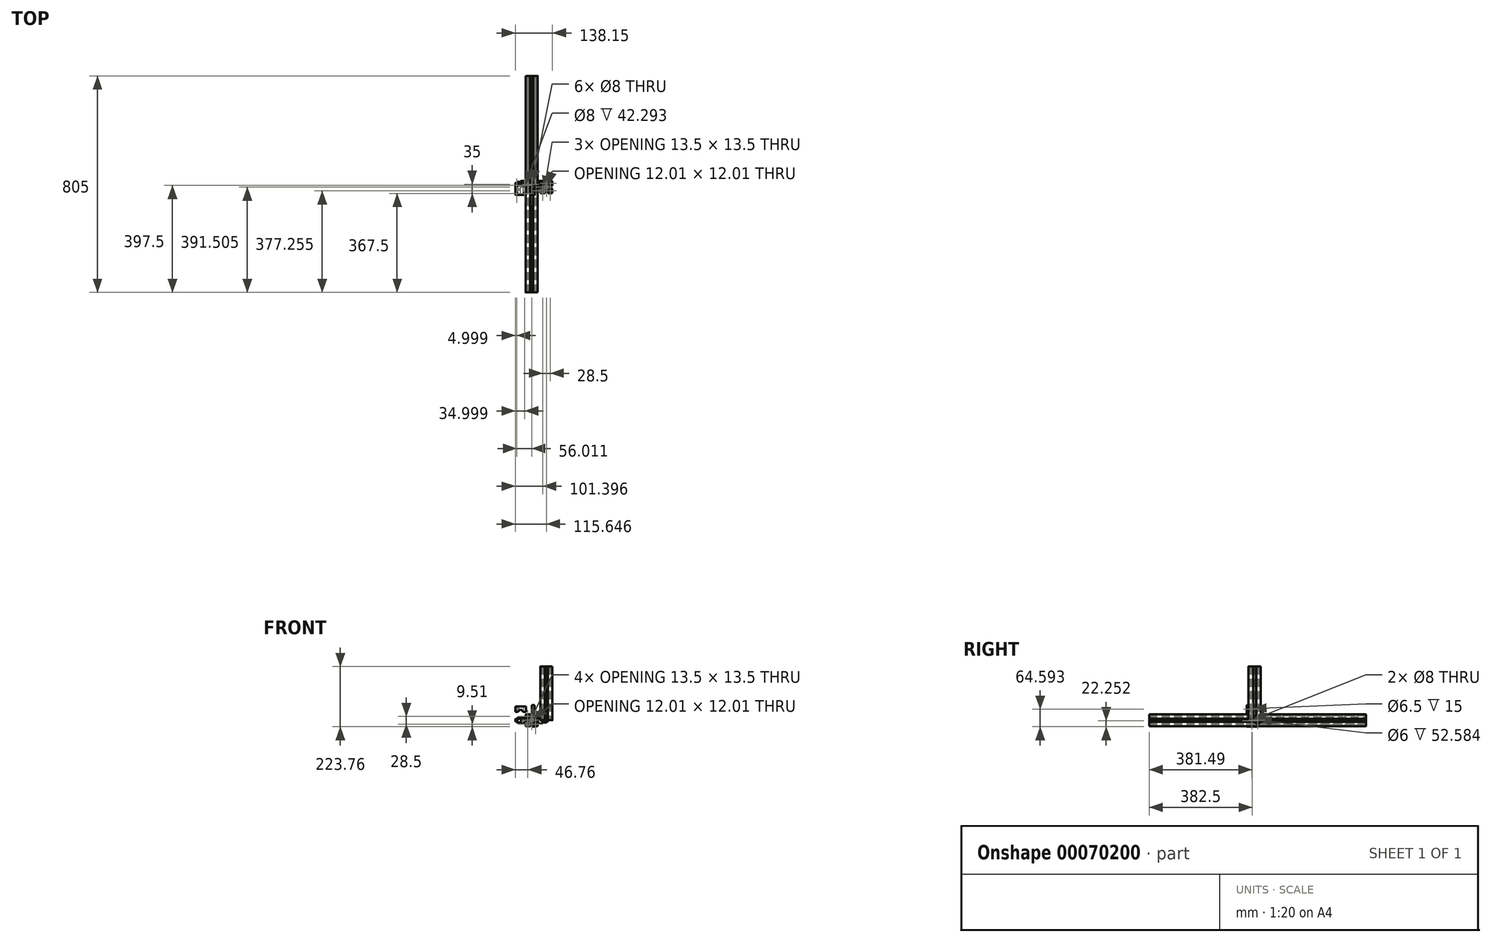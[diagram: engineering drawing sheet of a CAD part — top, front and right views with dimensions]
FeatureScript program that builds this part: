
annotation { "Feature Type Name" : "Feature", "Feature Type Description" : "" }
export const myFeature = defineFeature(function(context is Context, id is Id, definition is map)
    precondition{}
    {
        {
            var Q0;
            Q0=qCreatedBy(makeId("Front.planeOp"),FACE);
            var sketch = newSketch(context, id + "F0", { "sketchPlane" : qUnion([Q0])});
            skLineSegment(sketch, "E0", {"start": v(22.5, 19.5) * mm, "end": v(22.5, 5.8) * mm});
            skArc(sketch, "E1", {"start": v(-19.5, 22.5) * mm, "mid": v(-21.62, 21.62) * mm, "end": v(-22.5, 19.5) * mm});
            skArc(sketch, "E2", {"start": v(22.5, 19.5) * mm, "mid": v(21.62, 21.62) * mm, "end": v(19.5, 22.5) * mm});
            skLineSegment(sketch, "E3", {"start": v(-10.05, 16.5) * mm, "end": v(-5, 16.5) * mm});
            skLineSegment(sketch, "E4", {"start": v(-22.5, 5.8) * mm, "end": v(-22.5, 19.5) * mm});
            skLineSegment(sketch, "E5", {"start": v(-22.5, 5.8) * mm, "end": v(-21, 5.8) * mm});
            skLineSegment(sketch, "E6", {"start": v(-21, 5.8) * mm, "end": v(-21, 5) * mm});
            skLineSegment(sketch, "E7", {"start": v(-21, 5) * mm, "end": v(-16.5, 5) * mm});
            skLineSegment(sketch, "E8", {"start": v(-16.5, 5) * mm, "end": v(-16.5, 10.05) * mm});
            skLineSegment(sketch, "E9", {"start": v(-16.5, 10.05) * mm, "end": v(-11.68, 10.05) * mm});
            skLineSegment(sketch, "E10", {"start": v(-11.68, 10.05) * mm, "end": v(-6.41, 4.78) * mm});
            skArc(sketch, "E11", {"start": v(-6.41, 4.78) * mm, "mid": v(-8, 0) * mm, "end": v(-6.41, -4.78) * mm});
            skLineSegment(sketch, "E12", {"start": v(-6.41, -4.78) * mm, "end": v(-11.68, -10.05) * mm});
            skLineSegment(sketch, "E13", {"start": v(-11.68, -10.05) * mm, "end": v(-16.5, -10.05) * mm});
            skLineSegment(sketch, "E14", {"start": v(-16.5, -10.05) * mm, "end": v(-16.5, -5) * mm});
            skLineSegment(sketch, "E15", {"start": v(-16.5, -5) * mm, "end": v(-21, -5) * mm});
            skLineSegment(sketch, "E16", {"start": v(-21, -5) * mm, "end": v(-21, -5.8) * mm});
            skLineSegment(sketch, "E17", {"start": v(-21, -5.8) * mm, "end": v(-22.5, -5.8) * mm});
            skLineSegment(sketch, "E18", {"start": v(-22.5, -19.5) * mm, "end": v(-22.5, -5.8) * mm});
            skArc(sketch, "E19", {"start": v(-22.5, -19.5) * mm, "mid": v(-21.62, -21.62) * mm, "end": v(-19.5, -22.5) * mm});
            skLineSegment(sketch, "E20", {"start": v(-5.8, -22.5) * mm, "end": v(-19.5, -22.5) * mm});
            skLineSegment(sketch, "E21", {"start": v(-5.8, -22.5) * mm, "end": v(-5.8, -21) * mm});
            skLineSegment(sketch, "E22", {"start": v(-5.8, -21) * mm, "end": v(-5, -21) * mm});
            skLineSegment(sketch, "E23", {"start": v(-5, -21) * mm, "end": v(-5, -16.5) * mm});
            skLineSegment(sketch, "E24", {"start": v(-5, -16.5) * mm, "end": v(-10.05, -16.5) * mm});
            skLineSegment(sketch, "E25", {"start": v(-10.05, -16.5) * mm, "end": v(-10.05, -11.68) * mm});
            skLineSegment(sketch, "E26", {"start": v(-10.05, -11.68) * mm, "end": v(-4.78, -6.41) * mm});
            skArc(sketch, "E27", {"start": v(-4.78, -6.41) * mm, "mid": v(0, -8) * mm, "end": v(4.78, -6.41) * mm});
            skLineSegment(sketch, "E28", {"start": v(4.78, -6.41) * mm, "end": v(10.05, -11.68) * mm});
            skLineSegment(sketch, "E29", {"start": v(10.05, -11.68) * mm, "end": v(10.05, -16.5) * mm});
            skLineSegment(sketch, "E30", {"start": v(10.05, -16.5) * mm, "end": v(5, -16.5) * mm});
            skLineSegment(sketch, "E31", {"start": v(5, -16.5) * mm, "end": v(5, -21) * mm});
            skLineSegment(sketch, "E32", {"start": v(5, -21) * mm, "end": v(5.8, -21) * mm});
            skLineSegment(sketch, "E33", {"start": v(5.8, -21) * mm, "end": v(5.8, -22.5) * mm});
            skLineSegment(sketch, "E34", {"start": v(19.5, -22.5) * mm, "end": v(5.8, -22.5) * mm});
            skArc(sketch, "E35", {"start": v(19.5, -22.5) * mm, "mid": v(21.62, -21.62) * mm, "end": v(22.5, -19.5) * mm});
            skLineSegment(sketch, "E36", {"start": v(22.5, -5.8) * mm, "end": v(22.5, -19.5) * mm});
            skLineSegment(sketch, "E37", {"start": v(22.5, -5.8) * mm, "end": v(21, -5.8) * mm});
            skLineSegment(sketch, "E38", {"start": v(21, -5.8) * mm, "end": v(21, -5) * mm});
            skLineSegment(sketch, "E39", {"start": v(21, -5) * mm, "end": v(16.5, -5) * mm});
            skLineSegment(sketch, "E40", {"start": v(16.5, -5) * mm, "end": v(16.5, -10.05) * mm});
            skLineSegment(sketch, "E41", {"start": v(16.5, -10.05) * mm, "end": v(11.68, -10.05) * mm});
            skLineSegment(sketch, "E42", {"start": v(11.68, -10.05) * mm, "end": v(6.41, -4.78) * mm});
            skArc(sketch, "E43", {"start": v(6.41, -4.78) * mm, "mid": v(8, 0) * mm, "end": v(6.41, 4.78) * mm});
            skLineSegment(sketch, "E44", {"start": v(6.41, 4.78) * mm, "end": v(11.68, 10.05) * mm});
            skLineSegment(sketch, "E45", {"start": v(11.68, 10.05) * mm, "end": v(16.5, 10.05) * mm});
            skLineSegment(sketch, "E46", {"start": v(16.5, 10.05) * mm, "end": v(16.5, 5) * mm});
            skLineSegment(sketch, "E47", {"start": v(16.5, 5) * mm, "end": v(21, 5) * mm});
            skLineSegment(sketch, "E48", {"start": v(21, 5) * mm, "end": v(21, 5.8) * mm});
            skLineSegment(sketch, "E49", {"start": v(21, 5.8) * mm, "end": v(22.5, 5.8) * mm});
            skLineSegment(sketch, "E50", {"start": v(5, 16.5) * mm, "end": v(10.05, 16.5) * mm});
            skLineSegment(sketch, "E51", {"start": v(10.05, 16.5) * mm, "end": v(10.05, 11.68) * mm});
            skLineSegment(sketch, "E52", {"start": v(10.05, 11.68) * mm, "end": v(4.78, 6.41) * mm});
            skArc(sketch, "E53", {"start": v(4.78, 6.41) * mm, "mid": v(0, 8) * mm, "end": v(-4.78, 6.41) * mm});
            skLineSegment(sketch, "E54", {"start": v(-4.78, 6.41) * mm, "end": v(-10.05, 11.68) * mm});
            skLineSegment(sketch, "E55", {"start": v(-10.05, 11.68) * mm, "end": v(-10.05, 16.5) * mm});
            skLineSegment(sketch, "E56", {"start": v(21, 7.5) * mm, "end": v(18, 7.5) * mm});
            skLineSegment(sketch, "E57", {"start": v(18, 7.5) * mm, "end": v(18, 11.55) * mm});
            skLineSegment(sketch, "E58", {"start": v(18, 11.55) * mm, "end": v(11.55, 11.55) * mm});
            skLineSegment(sketch, "E59", {"start": v(11.55, 11.55) * mm, "end": v(11.55, 18) * mm});
            skLineSegment(sketch, "E60", {"start": v(11.55, 18) * mm, "end": v(7.5, 18) * mm});
            skLineSegment(sketch, "E61", {"start": v(7.5, 18) * mm, "end": v(7.5, 21) * mm});
            skLineSegment(sketch, "E62", {"start": v(7.5, 21) * mm, "end": v(18.5, 21) * mm});
            skArc(sketch, "E63", {"start": v(21, 18.5) * mm, "mid": v(20.27, 20.27) * mm, "end": v(18.5, 21) * mm});
            skLineSegment(sketch, "E64", {"start": v(21, 18.5) * mm, "end": v(21, 7.5) * mm});
            skLineSegment(sketch, "E65", {"start": v(7.5, -21) * mm, "end": v(7.5, -18) * mm});
            skLineSegment(sketch, "E66", {"start": v(7.5, -18) * mm, "end": v(11.55, -18) * mm});
            skLineSegment(sketch, "E67", {"start": v(11.55, -18) * mm, "end": v(11.55, -11.55) * mm});
            skLineSegment(sketch, "E68", {"start": v(11.55, -11.55) * mm, "end": v(18, -11.55) * mm});
            skLineSegment(sketch, "E69", {"start": v(18, -11.55) * mm, "end": v(18, -7.5) * mm});
            skLineSegment(sketch, "E70", {"start": v(18, -7.5) * mm, "end": v(21, -7.5) * mm});
            skLineSegment(sketch, "E71", {"start": v(21, -7.5) * mm, "end": v(21, -18.5) * mm});
            skArc(sketch, "E72", {"start": v(18.5, -21) * mm, "mid": v(20.27, -20.27) * mm, "end": v(21, -18.5) * mm});
            skLineSegment(sketch, "E73", {"start": v(18.5, -21) * mm, "end": v(7.5, -21) * mm});
            skLineSegment(sketch, "E74", {"start": v(-21, -7.5) * mm, "end": v(-18, -7.5) * mm});
            skLineSegment(sketch, "E75", {"start": v(-18, -7.5) * mm, "end": v(-18, -11.55) * mm});
            skLineSegment(sketch, "E76", {"start": v(-18, -11.55) * mm, "end": v(-11.55, -11.55) * mm});
            skLineSegment(sketch, "E77", {"start": v(-11.55, -11.55) * mm, "end": v(-11.55, -18) * mm});
            skLineSegment(sketch, "E78", {"start": v(-11.55, -18) * mm, "end": v(-7.5, -18) * mm});
            skLineSegment(sketch, "E79", {"start": v(-7.5, -18) * mm, "end": v(-7.5, -21) * mm});
            skLineSegment(sketch, "E80", {"start": v(-7.5, -21) * mm, "end": v(-18.5, -21) * mm});
            skArc(sketch, "E81", {"start": v(-21, -18.5) * mm, "mid": v(-20.27, -20.27) * mm, "end": v(-18.5, -21) * mm});
            skLineSegment(sketch, "E82", {"start": v(-21, -18.5) * mm, "end": v(-21, -7.5) * mm});
            skLineSegment(sketch, "E83", {"start": v(-7.5, 21) * mm, "end": v(-7.5, 18) * mm});
            skLineSegment(sketch, "E84", {"start": v(-7.5, 18) * mm, "end": v(-11.55, 18) * mm});
            skLineSegment(sketch, "E85", {"start": v(-11.55, 18) * mm, "end": v(-11.55, 11.55) * mm});
            skLineSegment(sketch, "E86", {"start": v(-11.55, 11.55) * mm, "end": v(-18, 11.55) * mm});
            skLineSegment(sketch, "E87", {"start": v(-18, 11.55) * mm, "end": v(-18, 7.5) * mm});
            skLineSegment(sketch, "E88", {"start": v(-18, 7.5) * mm, "end": v(-21, 7.5) * mm});
            skLineSegment(sketch, "E89", {"start": v(-21, 7.5) * mm, "end": v(-21, 18.5) * mm});
            skArc(sketch, "E90", {"start": v(-18.5, 21) * mm, "mid": v(-20.27, 20.27) * mm, "end": v(-21, 18.5) * mm});
            skLineSegment(sketch, "E91", {"start": v(-18.5, 21) * mm, "end": v(-7.5, 21) * mm});
            skArc(sketch, "E92", {"start": v(-5, 3.5) * mm, "mid": v(-5.64, 2.33) * mm, "end": v(-6, 1.06) * mm});
            skLineSegment(sketch, "E93", {"start": v(-5, 3.5) * mm, "end": v(-4.1, 2.87) * mm});
            skArc(sketch, "E94", {"start": v(-2.87, 4.1) * mm, "mid": v(-3.54, 3.54) * mm, "end": v(-4.1, 2.87) * mm});
            skLineSegment(sketch, "E95", {"start": v(-2.87, 4.1) * mm, "end": v(-3.5, 5) * mm});
            skArc(sketch, "E96", {"start": v(-1.06, 6) * mm, "mid": v(-2.33, 5.64) * mm, "end": v(-3.5, 5) * mm});
            skLineSegment(sketch, "E97", {"start": v(-1.06, 6) * mm, "end": v(-0.87, 4.92) * mm});
            skArc(sketch, "E98", {"start": v(0.87, 4.92) * mm, "mid": v(0, 5) * mm, "end": v(-0.87, 4.92) * mm});
            skLineSegment(sketch, "E99", {"start": v(0.87, 4.92) * mm, "end": v(1.06, 6) * mm});
            skArc(sketch, "E100", {"start": v(3.5, 5) * mm, "mid": v(2.33, 5.64) * mm, "end": v(1.06, 6) * mm});
            skLineSegment(sketch, "E101", {"start": v(3.5, 5) * mm, "end": v(2.87, 4.1) * mm});
            skArc(sketch, "E102", {"start": v(4.1, 2.87) * mm, "mid": v(3.54, 3.54) * mm, "end": v(2.87, 4.1) * mm});
            skLineSegment(sketch, "E103", {"start": v(4.1, 2.87) * mm, "end": v(5, 3.5) * mm});
            skArc(sketch, "E104", {"start": v(6, 1.06) * mm, "mid": v(5.64, 2.33) * mm, "end": v(5, 3.5) * mm});
            skLineSegment(sketch, "E105", {"start": v(6, 1.06) * mm, "end": v(4.92, 0.87) * mm});
            skArc(sketch, "E106", {"start": v(4.92, -0.87) * mm, "mid": v(5, 0) * mm, "end": v(4.92, 0.87) * mm});
            skLineSegment(sketch, "E107", {"start": v(4.92, -0.87) * mm, "end": v(6, -1.06) * mm});
            skArc(sketch, "E108", {"start": v(5, -3.5) * mm, "mid": v(5.64, -2.33) * mm, "end": v(6, -1.06) * mm});
            skLineSegment(sketch, "E109", {"start": v(5, -3.5) * mm, "end": v(4.1, -2.87) * mm});
            skArc(sketch, "E110", {"start": v(2.87, -4.1) * mm, "mid": v(3.54, -3.54) * mm, "end": v(4.1, -2.87) * mm});
            skLineSegment(sketch, "E111", {"start": v(2.87, -4.1) * mm, "end": v(3.5, -5) * mm});
            skArc(sketch, "E112", {"start": v(1.06, -6) * mm, "mid": v(2.33, -5.64) * mm, "end": v(3.5, -5) * mm});
            skLineSegment(sketch, "E113", {"start": v(1.06, -6) * mm, "end": v(0.87, -4.92) * mm});
            skArc(sketch, "E114", {"start": v(-0.87, -4.92) * mm, "mid": v(0, -5) * mm, "end": v(0.87, -4.92) * mm});
            skLineSegment(sketch, "E115", {"start": v(-0.87, -4.92) * mm, "end": v(-1.06, -6) * mm});
            skArc(sketch, "E116", {"start": v(-3.5, -5) * mm, "mid": v(-2.33, -5.64) * mm, "end": v(-1.06, -6) * mm});
            skLineSegment(sketch, "E117", {"start": v(-3.5, -5) * mm, "end": v(-2.87, -4.1) * mm});
            skArc(sketch, "E118", {"start": v(-4.1, -2.87) * mm, "mid": v(-3.54, -3.54) * mm, "end": v(-2.87, -4.1) * mm});
            skLineSegment(sketch, "E119", {"start": v(-4.1, -2.87) * mm, "end": v(-5, -3.5) * mm});
            skArc(sketch, "E120", {"start": v(-6, -1.06) * mm, "mid": v(-5.64, -2.33) * mm, "end": v(-5, -3.5) * mm});
            skLineSegment(sketch, "E121", {"start": v(-6, -1.06) * mm, "end": v(-4.92, -0.87) * mm});
            skArc(sketch, "E122", {"start": v(-4.92, 0.87) * mm, "mid": v(-5, 0) * mm, "end": v(-4.92, -0.87) * mm});
            skLineSegment(sketch, "E123", {"start": v(-4.92, 0.87) * mm, "end": v(-6, 1.06) * mm});
            skLineSegment(sketch, "E124.top", {"start": v(-5, 20.85) * mm, "end": v(-6, 20.85) * mm});
            skLineSegment(sketch, "E124.right", {"start": v(-6, 22.5) * mm, "end": v(-6, 20.85) * mm});
            skLineSegment(sketch, "E125.top", {"start": v(5, 20.85) * mm, "end": v(6, 20.85) * mm});
            skLineSegment(sketch, "E125.right", {"start": v(6, 22.5) * mm, "end": v(6, 20.85) * mm});
            skLineSegment(sketch, "E126", {"start": v(-19.5, 22.5) * mm, "end": v(-6, 22.5) * mm});
            skLineSegment(sketch, "E127", {"start": v(-5, 20.85) * mm, "end": v(-5, 16.5) * mm});
            skLineSegment(sketch, "E128", {"start": v(5, 20.85) * mm, "end": v(5, 16.5) * mm});
            skLineSegment(sketch, "E129", {"start": v(6, 22.5) * mm, "end": v(19.5, 22.5) * mm});
            skCircle(sketch, "E130", {"center": v(0, 0) * mm, "radius": 4 * mm});
            skSolve(sketch);
        }
        {
            var Q0;
            Q0=makeQuery(id+"F0.imprint","IMPRINT",FACE,{"disambiguationData":[TD([[makeQuery(id+"F0.imprint","IMPRINT",EDGE,{"derivedFrom":sQuery(id+"F0.wireOp",EDGE,"E0")}),-1.0]])]});
            extrude(context, id + "F1", {"entities" : qUnion([Q0]), "endBound" : BoundingType.SYMMETRIC, "depth" : 805 * mm});
        }
        {
            var Q0;
            Q0=qCreatedBy(makeId("Right.planeOp"),FACE);
            var sketch = newSketch(context, id + "F2", { "sketchPlane" : qUnion([Q0])});
            skLineSegment(sketch, "E131.bottom", {"start": v(-40.87, 56.24) * mm, "end": v(-0.87, 56.24) * mm});
            skLineSegment(sketch, "E131.top", {"start": v(-40.87, -23.76) * mm, "end": v(-0.87, -23.76) * mm});
            skLineSegment(sketch, "E131.left", {"start": v(-40.87, 56.24) * mm, "end": v(-40.87, -23.76) * mm});
            skLineSegment(sketch, "E131.right", {"start": v(-0.87, 56.24) * mm, "end": v(-0.87, -23.76) * mm});
            skLineSegment(sketch, "E132", {"start": v(-40.87, 3) * mm, "end": v(0, 3) * mm});
            skLineSegment(sketch, "E133", {"start": v(-40.87, -6.5) * mm, "end": v(-0.87, -6.5) * mm});
            skLineSegment(sketch, "E134.bottom", {"start": v(-25.77, 56.24) * mm, "end": v(-15.97, 56.24) * mm});
            skLineSegment(sketch, "E134.top", {"start": v(-25.77, 26.24) * mm, "end": v(-15.97, 26.24) * mm});
            skLineSegment(sketch, "E134.left", {"start": v(-25.77, 56.24) * mm, "end": v(-25.77, 26.24) * mm});
            skLineSegment(sketch, "E134.right", {"start": v(-15.97, 56.24) * mm, "end": v(-15.97, 26.24) * mm});
            skCircle(sketch, "E135", {"center": v(-20.87, 41.24) * mm, "radius": 4 * mm});
            skPoint(sketch, "E135.centerSnap0", {"position": v(-25.77, 41.24) * mm});
            skLineSegment(sketch, "E136", {"start": v(-20.87, 56.24) * mm, "end": v(-20.87, -7.98) * mm, "construction": true});
            skPoint(sketch, "E136.endSnap0", {"position": v(-20.87, 26.24) * mm});
            skCircle(sketch, "E137", {"center": v(-21, -1.5) * mm, "radius": 4 * mm});
            skLineSegment(sketch, "E138", {"start": v(-0.87, 33.08) * mm, "end": v(-15.97, 33.08) * mm, "construction": true});
            skLineSegment(sketch, "E139", {"start": v(-25.77, 32.73) * mm, "end": v(-40.87, 32.73) * mm, "construction": true});
            skSolve(sketch);
        }
        {
            var Q0;
            Q0=makeQuery(id+"F2.imprint","IMPRINT",FACE,{"disambiguationData":[TD([[makeQuery(id+"F2.imprint","IMPRINT",EDGE,{"derivedFrom":sQuery(id+"F2.wireOp",EDGE,"E134.bottom")}),-1.0]])]});
            var Q1;
            {var subQ0=sQuery(id+"F2.wireOp",EDGE,"E133");Q1=makeQuery(id+"F2.imprint","IMPRINT",FACE,{"disambiguationData":[TD([[makeQuery(id+"F2.imprint","IMPRINT",EDGE,{"derivedFrom":subQ0}),1.0]])]});}
            extrude(context, id + "F3", {"entities" : qUnion([Q0, Q1]), "depth" : 14 * mm});
        }
        {
            var Q0;
            {var subQ0=sQuery(id+"F2.wireOp",EDGE,"E131.top");Q0=makeQuery(id+"F2.imprint","IMPRINT",FACE,{"disambiguationData":[TD([[makeQuery(id+"F2.imprint","IMPRINT",EDGE,{"derivedFrom":subQ0}),1.0]])]});}
            var Q1;
            Q1=makeQuery(id+"F2.imprint","IMPRINT",FACE,{"disambiguationData":[TD([[makeQuery(id+"F2.imprint","IMPRINT",EDGE,{"derivedFrom":sQuery(id+"F2.wireOp",EDGE,"E134.top")}),-1.0]])]});
            extrude(context, id + "F4", {"entities" : qUnion([Q0, Q1]), "operationType" : NewBodyOperationType.ADD, "depth" : 10 * mm});
        }
        {
            var Q0;
            Q0=qCreatedBy(makeId("Top.planeOp"),FACE);
            var sketch = newSketch(context, id + "F5", { "sketchPlane" : qUnion([Q0])});
            skLineSegment(sketch, "E140", {"start": v(77.14, 8.5) * mm, "end": v(77.14, -5.2) * mm});
            skArc(sketch, "E141", {"start": v(35.14, 11.5) * mm, "mid": v(33.01, 10.63) * mm, "end": v(32.14, 8.5) * mm});
            skArc(sketch, "E142", {"start": v(77.14, 8.5) * mm, "mid": v(76.26, 10.63) * mm, "end": v(74.14, 11.5) * mm});
            skLineSegment(sketch, "E143", {"start": v(44.59, 5.5) * mm, "end": v(49.64, 5.5) * mm});
            skLineSegment(sketch, "E144", {"start": v(32.14, -5.2) * mm, "end": v(32.14, 8.5) * mm});
            skLineSegment(sketch, "E145", {"start": v(32.14, -5.2) * mm, "end": v(33.64, -5.2) * mm});
            skLineSegment(sketch, "E146", {"start": v(33.64, -5.2) * mm, "end": v(33.64, -6) * mm});
            skLineSegment(sketch, "E147", {"start": v(33.64, -6) * mm, "end": v(38.14, -6) * mm});
            skLineSegment(sketch, "E148", {"start": v(38.14, -6) * mm, "end": v(38.14, -0.95) * mm});
            skLineSegment(sketch, "E149", {"start": v(38.14, -0.95) * mm, "end": v(42.96, -0.95) * mm});
            skLineSegment(sketch, "E150", {"start": v(42.96, -0.95) * mm, "end": v(48.22, -6.21) * mm});
            skArc(sketch, "E151", {"start": v(48.22, -6.21) * mm, "mid": v(46.64, -11) * mm, "end": v(48.22, -15.78) * mm});
            skLineSegment(sketch, "E152", {"start": v(48.22, -15.78) * mm, "end": v(42.96, -21.05) * mm});
            skLineSegment(sketch, "E153", {"start": v(42.96, -21.05) * mm, "end": v(38.14, -21.05) * mm});
            skLineSegment(sketch, "E154", {"start": v(38.14, -21.05) * mm, "end": v(38.14, -16) * mm});
            skLineSegment(sketch, "E155", {"start": v(38.14, -16) * mm, "end": v(33.64, -16) * mm});
            skLineSegment(sketch, "E156", {"start": v(33.64, -16) * mm, "end": v(33.64, -16.8) * mm});
            skLineSegment(sketch, "E157", {"start": v(33.64, -16.8) * mm, "end": v(32.14, -16.8) * mm});
            skLineSegment(sketch, "E158", {"start": v(32.14, -30.5) * mm, "end": v(32.14, -16.8) * mm});
            skArc(sketch, "E159", {"start": v(32.14, -30.5) * mm, "mid": v(33.01, -32.62) * mm, "end": v(35.14, -33.5) * mm});
            skLineSegment(sketch, "E160", {"start": v(48.84, -33.5) * mm, "end": v(35.14, -33.5) * mm});
            skLineSegment(sketch, "E161", {"start": v(48.84, -33.5) * mm, "end": v(48.84, -32) * mm});
            skLineSegment(sketch, "E162", {"start": v(48.84, -32) * mm, "end": v(49.64, -32) * mm});
            skLineSegment(sketch, "E163", {"start": v(49.64, -32) * mm, "end": v(49.64, -27.5) * mm});
            skLineSegment(sketch, "E164", {"start": v(49.64, -27.5) * mm, "end": v(44.59, -27.5) * mm});
            skLineSegment(sketch, "E165", {"start": v(44.59, -27.5) * mm, "end": v(44.59, -22.67) * mm});
            skLineSegment(sketch, "E166", {"start": v(44.59, -22.67) * mm, "end": v(49.85, -17.4) * mm});
            skArc(sketch, "E167", {"start": v(49.85, -17.4) * mm, "mid": v(54.64, -19) * mm, "end": v(59.42, -17.4) * mm});
            skLineSegment(sketch, "E168", {"start": v(59.42, -17.4) * mm, "end": v(64.69, -22.67) * mm});
            skLineSegment(sketch, "E169", {"start": v(64.69, -22.67) * mm, "end": v(64.69, -27.5) * mm});
            skLineSegment(sketch, "E170", {"start": v(64.69, -27.5) * mm, "end": v(59.64, -27.5) * mm});
            skLineSegment(sketch, "E171", {"start": v(59.64, -27.5) * mm, "end": v(59.64, -32) * mm});
            skLineSegment(sketch, "E172", {"start": v(59.64, -32) * mm, "end": v(60.44, -32) * mm});
            skLineSegment(sketch, "E173", {"start": v(60.44, -32) * mm, "end": v(60.44, -33.5) * mm});
            skLineSegment(sketch, "E174", {"start": v(74.14, -33.5) * mm, "end": v(60.44, -33.5) * mm});
            skArc(sketch, "E175", {"start": v(74.14, -33.5) * mm, "mid": v(76.26, -32.62) * mm, "end": v(77.14, -30.5) * mm});
            skLineSegment(sketch, "E176", {"start": v(77.14, -16.8) * mm, "end": v(77.14, -30.5) * mm});
            skLineSegment(sketch, "E177", {"start": v(77.14, -16.8) * mm, "end": v(75.64, -16.8) * mm});
            skLineSegment(sketch, "E178", {"start": v(75.64, -16.8) * mm, "end": v(75.64, -16) * mm});
            skLineSegment(sketch, "E179", {"start": v(75.64, -16) * mm, "end": v(71.14, -16) * mm});
            skLineSegment(sketch, "E180", {"start": v(71.14, -16) * mm, "end": v(71.14, -21.05) * mm});
            skLineSegment(sketch, "E181", {"start": v(71.14, -21.05) * mm, "end": v(66.31, -21.05) * mm});
            skLineSegment(sketch, "E182", {"start": v(66.31, -21.05) * mm, "end": v(61.05, -15.78) * mm});
            skArc(sketch, "E183", {"start": v(61.05, -15.78) * mm, "mid": v(62.64, -11) * mm, "end": v(61.05, -6.21) * mm});
            skLineSegment(sketch, "E184", {"start": v(61.05, -6.21) * mm, "end": v(66.31, -0.95) * mm});
            skLineSegment(sketch, "E185", {"start": v(66.31, -0.95) * mm, "end": v(71.14, -0.95) * mm});
            skLineSegment(sketch, "E186", {"start": v(71.14, -0.95) * mm, "end": v(71.14, -6) * mm});
            skLineSegment(sketch, "E187", {"start": v(71.14, -6) * mm, "end": v(75.64, -6) * mm});
            skLineSegment(sketch, "E188", {"start": v(75.64, -6) * mm, "end": v(75.64, -5.2) * mm});
            skLineSegment(sketch, "E189", {"start": v(75.64, -5.2) * mm, "end": v(77.14, -5.2) * mm});
            skLineSegment(sketch, "E190", {"start": v(59.64, 5.5) * mm, "end": v(64.69, 5.5) * mm});
            skLineSegment(sketch, "E191", {"start": v(64.69, 5.5) * mm, "end": v(64.69, 0.68) * mm});
            skLineSegment(sketch, "E192", {"start": v(64.69, 0.68) * mm, "end": v(59.42, -4.58) * mm});
            skArc(sketch, "E193", {"start": v(59.42, -4.58) * mm, "mid": v(54.64, -3) * mm, "end": v(49.85, -4.58) * mm});
            skLineSegment(sketch, "E194", {"start": v(49.85, -4.58) * mm, "end": v(44.59, 0.68) * mm});
            skLineSegment(sketch, "E195", {"start": v(44.59, 0.68) * mm, "end": v(44.59, 5.5) * mm});
            skLineSegment(sketch, "E196", {"start": v(75.64, -3.5) * mm, "end": v(72.64, -3.5) * mm});
            skLineSegment(sketch, "E197", {"start": v(72.64, -3.5) * mm, "end": v(72.64, 0.55) * mm});
            skLineSegment(sketch, "E198", {"start": v(72.64, 0.55) * mm, "end": v(66.19, 0.55) * mm});
            skLineSegment(sketch, "E199", {"start": v(66.19, 0.55) * mm, "end": v(66.19, 7) * mm});
            skLineSegment(sketch, "E200", {"start": v(66.19, 7) * mm, "end": v(62.14, 7) * mm});
            skLineSegment(sketch, "E201", {"start": v(62.14, 7) * mm, "end": v(62.14, 10) * mm});
            skLineSegment(sketch, "E202", {"start": v(62.14, 10) * mm, "end": v(73.14, 10) * mm});
            skArc(sketch, "E203", {"start": v(75.64, 7.5) * mm, "mid": v(74.9, 9.27) * mm, "end": v(73.14, 10) * mm});
            skLineSegment(sketch, "E204", {"start": v(75.64, 7.5) * mm, "end": v(75.64, -3.5) * mm});
            skLineSegment(sketch, "E205", {"start": v(62.14, -32) * mm, "end": v(62.14, -29) * mm});
            skLineSegment(sketch, "E206", {"start": v(62.14, -29) * mm, "end": v(66.19, -29) * mm});
            skLineSegment(sketch, "E207", {"start": v(66.19, -29) * mm, "end": v(66.19, -22.55) * mm});
            skLineSegment(sketch, "E208", {"start": v(66.19, -22.55) * mm, "end": v(72.64, -22.55) * mm});
            skLineSegment(sketch, "E209", {"start": v(72.64, -22.55) * mm, "end": v(72.64, -18.5) * mm});
            skLineSegment(sketch, "E210", {"start": v(72.64, -18.5) * mm, "end": v(75.64, -18.5) * mm});
            skLineSegment(sketch, "E211", {"start": v(75.64, -18.5) * mm, "end": v(75.64, -29.5) * mm});
            skArc(sketch, "E212", {"start": v(73.14, -32) * mm, "mid": v(74.9, -31.26) * mm, "end": v(75.64, -29.5) * mm});
            skLineSegment(sketch, "E213", {"start": v(73.14, -32) * mm, "end": v(62.14, -32) * mm});
            skLineSegment(sketch, "E214", {"start": v(33.64, -18.5) * mm, "end": v(36.64, -18.5) * mm});
            skLineSegment(sketch, "E215", {"start": v(36.64, -18.5) * mm, "end": v(36.64, -22.55) * mm});
            skLineSegment(sketch, "E216", {"start": v(36.64, -22.55) * mm, "end": v(43.09, -22.55) * mm});
            skLineSegment(sketch, "E217", {"start": v(43.09, -22.55) * mm, "end": v(43.09, -29) * mm});
            skLineSegment(sketch, "E218", {"start": v(43.09, -29) * mm, "end": v(47.14, -29) * mm});
            skLineSegment(sketch, "E219", {"start": v(47.14, -29) * mm, "end": v(47.14, -32) * mm});
            skLineSegment(sketch, "E220", {"start": v(47.14, -32) * mm, "end": v(36.14, -32) * mm});
            skArc(sketch, "E221", {"start": v(33.64, -29.5) * mm, "mid": v(34.37, -31.26) * mm, "end": v(36.14, -32) * mm});
            skLineSegment(sketch, "E222", {"start": v(33.64, -29.5) * mm, "end": v(33.64, -18.5) * mm});
            skLineSegment(sketch, "E223", {"start": v(47.14, 10) * mm, "end": v(47.14, 7) * mm});
            skLineSegment(sketch, "E224", {"start": v(47.14, 7) * mm, "end": v(43.09, 7) * mm});
            skLineSegment(sketch, "E225", {"start": v(43.09, 7) * mm, "end": v(43.09, 0.55) * mm});
            skLineSegment(sketch, "E226", {"start": v(43.09, 0.55) * mm, "end": v(36.64, 0.55) * mm});
            skLineSegment(sketch, "E227", {"start": v(36.64, 0.55) * mm, "end": v(36.64, -3.5) * mm});
            skLineSegment(sketch, "E228", {"start": v(36.64, -3.5) * mm, "end": v(33.64, -3.5) * mm});
            skLineSegment(sketch, "E229", {"start": v(33.64, -3.5) * mm, "end": v(33.64, 7.5) * mm});
            skArc(sketch, "E230", {"start": v(36.14, 10) * mm, "mid": v(34.37, 9.27) * mm, "end": v(33.64, 7.5) * mm});
            skLineSegment(sketch, "E231", {"start": v(36.14, 10) * mm, "end": v(47.14, 10) * mm});
            skArc(sketch, "E232", {"start": v(49.64, -7.5) * mm, "mid": v(49, -8.66) * mm, "end": v(48.63, -9.94) * mm});
            skLineSegment(sketch, "E233", {"start": v(49.64, -7.5) * mm, "end": v(50.54, -8.13) * mm});
            skArc(sketch, "E234", {"start": v(51.77, -6.9) * mm, "mid": v(51.1, -7.46) * mm, "end": v(50.54, -8.13) * mm});
            skLineSegment(sketch, "E235", {"start": v(51.77, -6.9) * mm, "end": v(51.14, -6) * mm});
            skArc(sketch, "E236", {"start": v(53.58, -4.99) * mm, "mid": v(52.3, -5.36) * mm, "end": v(51.14, -6) * mm});
            skLineSegment(sketch, "E237", {"start": v(53.58, -4.99) * mm, "end": v(53.77, -6.07) * mm});
            skArc(sketch, "E238", {"start": v(55.5, -6.07) * mm, "mid": v(54.64, -6) * mm, "end": v(53.77, -6.07) * mm});
            skLineSegment(sketch, "E239", {"start": v(55.5, -6.07) * mm, "end": v(55.7, -4.99) * mm});
            skArc(sketch, "E240", {"start": v(58.13, -6) * mm, "mid": v(56.97, -5.36) * mm, "end": v(55.7, -4.99) * mm});
            skLineSegment(sketch, "E241", {"start": v(58.13, -6) * mm, "end": v(57.5, -6.9) * mm});
            skArc(sketch, "E242", {"start": v(58.73, -8.13) * mm, "mid": v(58.17, -7.46) * mm, "end": v(57.5, -6.9) * mm});
            skLineSegment(sketch, "E243", {"start": v(58.73, -8.13) * mm, "end": v(59.63, -7.5) * mm});
            skArc(sketch, "E244", {"start": v(60.64, -9.94) * mm, "mid": v(60.27, -8.66) * mm, "end": v(59.63, -7.5) * mm});
            skLineSegment(sketch, "E245", {"start": v(60.64, -9.94) * mm, "end": v(59.56, -10.13) * mm});
            skArc(sketch, "E246", {"start": v(59.56, -11.86) * mm, "mid": v(59.64, -11) * mm, "end": v(59.56, -10.13) * mm});
            skLineSegment(sketch, "E247", {"start": v(59.56, -11.86) * mm, "end": v(60.64, -12.05) * mm});
            skArc(sketch, "E248", {"start": v(59.63, -14.5) * mm, "mid": v(60.27, -13.33) * mm, "end": v(60.64, -12.05) * mm});
            skLineSegment(sketch, "E249", {"start": v(59.63, -14.5) * mm, "end": v(58.73, -13.86) * mm});
            skArc(sketch, "E250", {"start": v(57.5, -15.1) * mm, "mid": v(58.17, -14.53) * mm, "end": v(58.73, -13.86) * mm});
            skLineSegment(sketch, "E251", {"start": v(57.5, -15.1) * mm, "end": v(58.13, -16) * mm});
            skArc(sketch, "E252", {"start": v(55.7, -17) * mm, "mid": v(56.97, -16.63) * mm, "end": v(58.13, -16) * mm});
            skLineSegment(sketch, "E253", {"start": v(55.7, -17) * mm, "end": v(55.5, -15.92) * mm});
            skArc(sketch, "E254", {"start": v(53.77, -15.92) * mm, "mid": v(54.64, -16) * mm, "end": v(55.5, -15.92) * mm});
            skLineSegment(sketch, "E255", {"start": v(53.77, -15.92) * mm, "end": v(53.58, -17) * mm});
            skArc(sketch, "E256", {"start": v(51.14, -16) * mm, "mid": v(52.3, -16.63) * mm, "end": v(53.58, -17) * mm});
            skLineSegment(sketch, "E257", {"start": v(51.14, -16) * mm, "end": v(51.77, -15.1) * mm});
            skArc(sketch, "E258", {"start": v(50.54, -13.86) * mm, "mid": v(51.1, -14.53) * mm, "end": v(51.77, -15.1) * mm});
            skLineSegment(sketch, "E259", {"start": v(50.54, -13.86) * mm, "end": v(49.64, -14.5) * mm});
            skArc(sketch, "E260", {"start": v(48.63, -12.05) * mm, "mid": v(49, -13.33) * mm, "end": v(49.64, -14.5) * mm});
            skLineSegment(sketch, "E261", {"start": v(48.63, -12.05) * mm, "end": v(49.71, -11.86) * mm});
            skArc(sketch, "E262", {"start": v(49.71, -10.13) * mm, "mid": v(49.64, -11) * mm, "end": v(49.71, -11.86) * mm});
            skLineSegment(sketch, "E263", {"start": v(49.71, -10.13) * mm, "end": v(48.63, -9.94) * mm});
            skLineSegment(sketch, "E264.top", {"start": v(49.64, 9.86) * mm, "end": v(48.63, 9.86) * mm});
            skLineSegment(sketch, "E264.right", {"start": v(48.63, 11.5) * mm, "end": v(48.63, 9.86) * mm});
            skLineSegment(sketch, "E265.top", {"start": v(59.64, 9.86) * mm, "end": v(60.65, 9.86) * mm});
            skLineSegment(sketch, "E265.right", {"start": v(60.65, 11.5) * mm, "end": v(60.65, 9.86) * mm});
            skLineSegment(sketch, "E266", {"start": v(35.14, 11.5) * mm, "end": v(48.63, 11.5) * mm});
            skLineSegment(sketch, "E267", {"start": v(49.64, 9.86) * mm, "end": v(49.64, 5.5) * mm});
            skLineSegment(sketch, "E268", {"start": v(59.64, 9.86) * mm, "end": v(59.64, 5.5) * mm});
            skLineSegment(sketch, "E269", {"start": v(60.65, 11.5) * mm, "end": v(74.14, 11.5) * mm});
            skCircle(sketch, "E270", {"center": v(54.64, -11) * mm, "radius": 4 * mm});
            skSolve(sketch);
        }
        {
            var Q0;
            Q0=makeQuery(id+"F5.imprint","IMPRINT",FACE,{"disambiguationData":[TD([[makeQuery(id+"F5.imprint","IMPRINT",EDGE,{"derivedFrom":sQuery(id+"F5.wireOp",EDGE,"E140")}),-1.0]])]});
            extrude(context, id + "F6", {"entities" : qUnion([Q0]), "depth" : 200 * mm});
        }
        {
            var Q0;
            Q0=qCreatedBy(makeId("Right.planeOp"),FACE);
            var sketch = newSketch(context, id + "F7", { "sketchPlane" : qUnion([Q0])});
            skCircle(sketch, "E271", {"center": v(0, 0) * mm, "radius": 5 * mm});
            skCircle(sketch, "E272", {"center": v(0, 0) * mm, "radius": 8 * mm});
            skCircle(sketch, "E273", {"center": v(0, 0) * mm, "radius": 12.5 * mm});
            skCircle(sketch, "E274", {"center": v(0, 0) * mm, "radius": 3 * mm});
            skSolve(sketch);
        }
        {
            var Q0;
            Q0=makeQuery(id+"F7.imprint","IMPRINT",FACE,{"disambiguationData":[TD([[makeQuery(id+"F7.imprint","IMPRINT",EDGE,{"derivedFrom":sQuery(id+"F7.wireOp",EDGE,"E271")}),1.0]])]});
            extrude(context, id + "F8", {"entities" : qUnion([Q0]), "endBound" : BoundingType.SYMMETRIC, "depth" : 120 * mm});
        }
        {
            var Q0;
            Q0=makeQuery(id+"F7.imprint","IMPRINT",FACE,{"disambiguationData":[TD([[makeQuery(id+"F7.imprint","IMPRINT",EDGE,{"derivedFrom":sQuery(id+"F7.wireOp",EDGE,"E271")}),-1.0]])]});
            extrude(context, id + "F9", {"entities" : qUnion([Q0]), "operationType" : NewBodyOperationType.ADD, "endBound" : BoundingType.SYMMETRIC, "depth" : 110 * mm});
        }
        {
            var Q0;
            Q0=qCreatedBy(makeId("Front.planeOp"),FACE);
            var sketch = newSketch(context, id + "F10", { "sketchPlane" : qUnion([Q0])});
            skCircle(sketch, "E275", {"center": v(0, 0) * mm, "radius": 4 * mm});
            skLineSegment(sketch, "E276", {"start": v(-5, 0) * mm, "end": v(-4, 0) * mm, "construction": true});
            skSolve(sketch);
        }
        {
            var Q0;
            Q0=qCreatedBy(makeId("Top.planeOp"),FACE);
            var sketch = newSketch(context, id + "F11", { "sketchPlane" : qUnion([Q0])});
            skLineSegment(sketch, "E277", {"start": v(-21.8, -6) * mm, "end": v(23.24, -6) * mm});
            skLineSegment(sketch, "E278", {"start": v(23.24, -6) * mm, "end": v(23.24, -13) * mm});
            skLineSegment(sketch, "E279", {"start": v(23.24, -13) * mm, "end": v(-21.8, -13) * mm});
            skLineSegment(sketch, "E280", {"start": v(-21.8, -13) * mm, "end": v(-21.8, -6) * mm});
            skLineSegment(sketch, "E281", {"start": v(-4.98, -13) * mm, "end": v(-4.98, -6) * mm});
            skLineSegment(sketch, "E282", {"start": v(5.02, -6) * mm, "end": v(5.02, -13) * mm});
            skSolve(sketch);
        }
        {
            var Q0;
            Q0=makeQuery(id+"F7.imprint","IMPRINT",FACE,{"disambiguationData":[TD([[makeQuery(id+"F7.imprint","IMPRINT",EDGE,{"derivedFrom":sQuery(id+"F7.wireOp",EDGE,"E272")}),-1.0]])]});
            extrude(context, id + "F12", {"entities" : qUnion([Q0]), "operationType" : NewBodyOperationType.ADD, "endBound" : BoundingType.SYMMETRIC, "depth" : 80 * mm});
        }
        {
            var Q0;
            {var subQ0=sQuery(id+"F11.wireOp",EDGE,"E280");Q0=makeQuery(id+"F11.imprint","IMPRINT",FACE,{"disambiguationData":[TD([[makeQuery(id+"F11.imprint","IMPRINT",EDGE,{"derivedFrom":subQ0}),-1.0]])]});}
            var Q1;
            {var subQ0=sQuery(id+"F11.wireOp",EDGE,"E278");Q1=makeQuery(id+"F11.imprint","IMPRINT",FACE,{"disambiguationData":[TD([[makeQuery(id+"F11.imprint","IMPRINT",EDGE,{"derivedFrom":subQ0}),-1.0]])]});}
            extrude(context, id + "F13", {"entities" : qUnion([Q0, Q1]), "operationType" : NewBodyOperationType.REMOVE, "endBound" : BoundingType.THROUGH_ALL, "depth" : 25 * mm, "hasSecondDirection" : true, "secondDirectionBound" : SecondDirectionBoundingType.THROUGH_ALL, "secondDirectionOppositeDirection" : true, "secondDirectionDepth" : 25 * mm});
        }
        {
            var Q0;
            Q0 = qSketchRegion(id + "F10", true);
            extrude(context, id + "F14", {"entities" : qUnion([Q0]), "operationType" : NewBodyOperationType.REMOVE, "endBound" : BoundingType.THROUGH_ALL, "oppositeDirection" : true, "depth" : 25 * mm, "hasSecondDirection" : true, "secondDirectionBound" : SecondDirectionBoundingType.THROUGH_ALL, "secondDirectionOppositeDirection" : false, "secondDirectionDepth" : 25 * mm});
        }
        {
            var Q0;
            Q0=makeQuery(id+"F1.opExtrude","SWEPT_BODY",BODY,{"disambiguationData":[OSD([sQuery(id+"F0.wireOp",EDGE,"E0"),sQuery(id+"F0.wireOp",EDGE,"E1"),sQuery(id+"F0.wireOp",EDGE,"E2"),sQuery(id+"F0.wireOp",EDGE,"E3"),sQuery(id+"F0.wireOp",EDGE,"E4"),sQuery(id+"F0.wireOp",EDGE,"E5"),sQuery(id+"F0.wireOp",EDGE,"E6"),sQuery(id+"F0.wireOp",EDGE,"E7"),sQuery(id+"F0.wireOp",EDGE,"E8"),sQuery(id+"F0.wireOp",EDGE,"E9"),sQuery(id+"F0.wireOp",EDGE,"E10"),sQuery(id+"F0.wireOp",EDGE,"E11"),sQuery(id+"F0.wireOp",EDGE,"E12"),sQuery(id+"F0.wireOp",EDGE,"E13"),sQuery(id+"F0.wireOp",EDGE,"E14"),sQuery(id+"F0.wireOp",EDGE,"E15"),sQuery(id+"F0.wireOp",EDGE,"E16"),sQuery(id+"F0.wireOp",EDGE,"E17"),sQuery(id+"F0.wireOp",EDGE,"E18"),sQuery(id+"F0.wireOp",EDGE,"E19"),sQuery(id+"F0.wireOp",EDGE,"E20"),sQuery(id+"F0.wireOp",EDGE,"E21"),sQuery(id+"F0.wireOp",EDGE,"E22"),sQuery(id+"F0.wireOp",EDGE,"E23"),sQuery(id+"F0.wireOp",EDGE,"E24"),sQuery(id+"F0.wireOp",EDGE,"E25"),sQuery(id+"F0.wireOp",EDGE,"E26"),sQuery(id+"F0.wireOp",EDGE,"E27"),sQuery(id+"F0.wireOp",EDGE,"E28"),sQuery(id+"F0.wireOp",EDGE,"E29"),sQuery(id+"F0.wireOp",EDGE,"E30"),sQuery(id+"F0.wireOp",EDGE,"E31"),sQuery(id+"F0.wireOp",EDGE,"E32"),sQuery(id+"F0.wireOp",EDGE,"E33"),sQuery(id+"F0.wireOp",EDGE,"E34"),sQuery(id+"F0.wireOp",EDGE,"E35"),sQuery(id+"F0.wireOp",EDGE,"E36"),sQuery(id+"F0.wireOp",EDGE,"E37"),sQuery(id+"F0.wireOp",EDGE,"E38"),sQuery(id+"F0.wireOp",EDGE,"E39"),sQuery(id+"F0.wireOp",EDGE,"E40"),sQuery(id+"F0.wireOp",EDGE,"E41"),sQuery(id+"F0.wireOp",EDGE,"E42"),sQuery(id+"F0.wireOp",EDGE,"E43"),sQuery(id+"F0.wireOp",EDGE,"E44"),sQuery(id+"F0.wireOp",EDGE,"E45"),sQuery(id+"F0.wireOp",EDGE,"E46"),sQuery(id+"F0.wireOp",EDGE,"E47"),sQuery(id+"F0.wireOp",EDGE,"E48"),sQuery(id+"F0.wireOp",EDGE,"E49"),sQuery(id+"F0.wireOp",EDGE,"E50"),sQuery(id+"F0.wireOp",EDGE,"E51"),sQuery(id+"F0.wireOp",EDGE,"E52"),sQuery(id+"F0.wireOp",EDGE,"E53"),sQuery(id+"F0.wireOp",EDGE,"E54"),sQuery(id+"F0.wireOp",EDGE,"E55"),sQuery(id+"F0.wireOp",EDGE,"E56"),sQuery(id+"F0.wireOp",EDGE,"E57"),sQuery(id+"F0.wireOp",EDGE,"E58"),sQuery(id+"F0.wireOp",EDGE,"E59"),sQuery(id+"F0.wireOp",EDGE,"E60"),sQuery(id+"F0.wireOp",EDGE,"E61"),sQuery(id+"F0.wireOp",EDGE,"E62"),sQuery(id+"F0.wireOp",EDGE,"E63"),sQuery(id+"F0.wireOp",EDGE,"E64"),sQuery(id+"F0.wireOp",EDGE,"E65"),sQuery(id+"F0.wireOp",EDGE,"E66"),sQuery(id+"F0.wireOp",EDGE,"E67"),sQuery(id+"F0.wireOp",EDGE,"E68"),sQuery(id+"F0.wireOp",EDGE,"E69"),sQuery(id+"F0.wireOp",EDGE,"E70"),sQuery(id+"F0.wireOp",EDGE,"E71"),sQuery(id+"F0.wireOp",EDGE,"E72"),sQuery(id+"F0.wireOp",EDGE,"E73"),sQuery(id+"F0.wireOp",EDGE,"E74"),sQuery(id+"F0.wireOp",EDGE,"E75"),sQuery(id+"F0.wireOp",EDGE,"E76"),sQuery(id+"F0.wireOp",EDGE,"E77"),sQuery(id+"F0.wireOp",EDGE,"E78"),sQuery(id+"F0.wireOp",EDGE,"E79"),sQuery(id+"F0.wireOp",EDGE,"E80"),sQuery(id+"F0.wireOp",EDGE,"E81"),sQuery(id+"F0.wireOp",EDGE,"E82"),sQuery(id+"F0.wireOp",EDGE,"E83"),sQuery(id+"F0.wireOp",EDGE,"E84"),sQuery(id+"F0.wireOp",EDGE,"E85"),sQuery(id+"F0.wireOp",EDGE,"E86"),sQuery(id+"F0.wireOp",EDGE,"E87"),sQuery(id+"F0.wireOp",EDGE,"E88"),sQuery(id+"F0.wireOp",EDGE,"E89"),sQuery(id+"F0.wireOp",EDGE,"E90"),sQuery(id+"F0.wireOp",EDGE,"E91"),sQuery(id+"F0.wireOp",EDGE,"E92"),sQuery(id+"F0.wireOp",EDGE,"E93"),sQuery(id+"F0.wireOp",EDGE,"E94"),sQuery(id+"F0.wireOp",EDGE,"E95"),sQuery(id+"F0.wireOp",EDGE,"E96"),sQuery(id+"F0.wireOp",EDGE,"E97"),sQuery(id+"F0.wireOp",EDGE,"E98"),sQuery(id+"F0.wireOp",EDGE,"E99"),sQuery(id+"F0.wireOp",EDGE,"E100"),sQuery(id+"F0.wireOp",EDGE,"E101"),sQuery(id+"F0.wireOp",EDGE,"E102"),sQuery(id+"F0.wireOp",EDGE,"E103"),sQuery(id+"F0.wireOp",EDGE,"E104"),sQuery(id+"F0.wireOp",EDGE,"E105"),sQuery(id+"F0.wireOp",EDGE,"E106"),sQuery(id+"F0.wireOp",EDGE,"E107"),sQuery(id+"F0.wireOp",EDGE,"E108"),sQuery(id+"F0.wireOp",EDGE,"E109"),sQuery(id+"F0.wireOp",EDGE,"E110"),sQuery(id+"F0.wireOp",EDGE,"E111"),sQuery(id+"F0.wireOp",EDGE,"E112"),sQuery(id+"F0.wireOp",EDGE,"E113"),sQuery(id+"F0.wireOp",EDGE,"E114"),sQuery(id+"F0.wireOp",EDGE,"E115"),sQuery(id+"F0.wireOp",EDGE,"E116"),sQuery(id+"F0.wireOp",EDGE,"E117"),sQuery(id+"F0.wireOp",EDGE,"E118"),sQuery(id+"F0.wireOp",EDGE,"E119"),sQuery(id+"F0.wireOp",EDGE,"E120"),sQuery(id+"F0.wireOp",EDGE,"E121"),sQuery(id+"F0.wireOp",EDGE,"E122"),sQuery(id+"F0.wireOp",EDGE,"E123"),sQuery(id+"F0.wireOp",EDGE,"E124.top"),sQuery(id+"F0.wireOp",EDGE,"E124.right"),sQuery(id+"F0.wireOp",EDGE,"E125.top"),sQuery(id+"F0.wireOp",EDGE,"E125.right"),sQuery(id+"F0.wireOp",EDGE,"E126"),sQuery(id+"F0.wireOp",EDGE,"E127"),sQuery(id+"F0.wireOp",EDGE,"E128"),sQuery(id+"F0.wireOp",EDGE,"E129")])]});
            transform(context, id + "F15", {"entities" : qUnion([Q0]), "transformType" : TransformType.TRANSLATION_3D, "dx" : 125.05 * mm, "dy" : 0 * mm, "dz" : 0 * mm, "makeCopy" : true});
        }
        {
            var Q0;
            Q0=makeQuery(id+"F15.opPattern","COPY",BODY,{"derivedFrom":makeQuery(id+"F1.opExtrude","SWEPT_BODY",BODY,{"disambiguationData":[OSD([sQuery(id+"F0.wireOp",EDGE,"E0"),sQuery(id+"F0.wireOp",EDGE,"E1"),sQuery(id+"F0.wireOp",EDGE,"E2"),sQuery(id+"F0.wireOp",EDGE,"E3"),sQuery(id+"F0.wireOp",EDGE,"E4"),sQuery(id+"F0.wireOp",EDGE,"E5"),sQuery(id+"F0.wireOp",EDGE,"E6"),sQuery(id+"F0.wireOp",EDGE,"E7"),sQuery(id+"F0.wireOp",EDGE,"E8"),sQuery(id+"F0.wireOp",EDGE,"E9"),sQuery(id+"F0.wireOp",EDGE,"E10"),sQuery(id+"F0.wireOp",EDGE,"E11"),sQuery(id+"F0.wireOp",EDGE,"E12"),sQuery(id+"F0.wireOp",EDGE,"E13"),sQuery(id+"F0.wireOp",EDGE,"E14"),sQuery(id+"F0.wireOp",EDGE,"E15"),sQuery(id+"F0.wireOp",EDGE,"E16"),sQuery(id+"F0.wireOp",EDGE,"E17"),sQuery(id+"F0.wireOp",EDGE,"E18"),sQuery(id+"F0.wireOp",EDGE,"E19"),sQuery(id+"F0.wireOp",EDGE,"E20"),sQuery(id+"F0.wireOp",EDGE,"E21"),sQuery(id+"F0.wireOp",EDGE,"E22"),sQuery(id+"F0.wireOp",EDGE,"E23"),sQuery(id+"F0.wireOp",EDGE,"E24"),sQuery(id+"F0.wireOp",EDGE,"E25"),sQuery(id+"F0.wireOp",EDGE,"E26"),sQuery(id+"F0.wireOp",EDGE,"E27"),sQuery(id+"F0.wireOp",EDGE,"E28"),sQuery(id+"F0.wireOp",EDGE,"E29"),sQuery(id+"F0.wireOp",EDGE,"E30"),sQuery(id+"F0.wireOp",EDGE,"E31"),sQuery(id+"F0.wireOp",EDGE,"E32"),sQuery(id+"F0.wireOp",EDGE,"E33"),sQuery(id+"F0.wireOp",EDGE,"E34"),sQuery(id+"F0.wireOp",EDGE,"E35"),sQuery(id+"F0.wireOp",EDGE,"E36"),sQuery(id+"F0.wireOp",EDGE,"E37"),sQuery(id+"F0.wireOp",EDGE,"E38"),sQuery(id+"F0.wireOp",EDGE,"E39"),sQuery(id+"F0.wireOp",EDGE,"E40"),sQuery(id+"F0.wireOp",EDGE,"E41"),sQuery(id+"F0.wireOp",EDGE,"E42"),sQuery(id+"F0.wireOp",EDGE,"E43"),sQuery(id+"F0.wireOp",EDGE,"E44"),sQuery(id+"F0.wireOp",EDGE,"E45"),sQuery(id+"F0.wireOp",EDGE,"E46"),sQuery(id+"F0.wireOp",EDGE,"E47"),sQuery(id+"F0.wireOp",EDGE,"E48"),sQuery(id+"F0.wireOp",EDGE,"E49"),sQuery(id+"F0.wireOp",EDGE,"E50"),sQuery(id+"F0.wireOp",EDGE,"E51"),sQuery(id+"F0.wireOp",EDGE,"E52"),sQuery(id+"F0.wireOp",EDGE,"E53"),sQuery(id+"F0.wireOp",EDGE,"E54"),sQuery(id+"F0.wireOp",EDGE,"E55"),sQuery(id+"F0.wireOp",EDGE,"E56"),sQuery(id+"F0.wireOp",EDGE,"E57"),sQuery(id+"F0.wireOp",EDGE,"E58"),sQuery(id+"F0.wireOp",EDGE,"E59"),sQuery(id+"F0.wireOp",EDGE,"E60"),sQuery(id+"F0.wireOp",EDGE,"E61"),sQuery(id+"F0.wireOp",EDGE,"E62"),sQuery(id+"F0.wireOp",EDGE,"E63"),sQuery(id+"F0.wireOp",EDGE,"E64"),sQuery(id+"F0.wireOp",EDGE,"E65"),sQuery(id+"F0.wireOp",EDGE,"E66"),sQuery(id+"F0.wireOp",EDGE,"E67"),sQuery(id+"F0.wireOp",EDGE,"E68"),sQuery(id+"F0.wireOp",EDGE,"E69"),sQuery(id+"F0.wireOp",EDGE,"E70"),sQuery(id+"F0.wireOp",EDGE,"E71"),sQuery(id+"F0.wireOp",EDGE,"E72"),sQuery(id+"F0.wireOp",EDGE,"E73"),sQuery(id+"F0.wireOp",EDGE,"E74"),sQuery(id+"F0.wireOp",EDGE,"E75"),sQuery(id+"F0.wireOp",EDGE,"E76"),sQuery(id+"F0.wireOp",EDGE,"E77"),sQuery(id+"F0.wireOp",EDGE,"E78"),sQuery(id+"F0.wireOp",EDGE,"E79"),sQuery(id+"F0.wireOp",EDGE,"E80"),sQuery(id+"F0.wireOp",EDGE,"E81"),sQuery(id+"F0.wireOp",EDGE,"E82"),sQuery(id+"F0.wireOp",EDGE,"E83"),sQuery(id+"F0.wireOp",EDGE,"E84"),sQuery(id+"F0.wireOp",EDGE,"E85"),sQuery(id+"F0.wireOp",EDGE,"E86"),sQuery(id+"F0.wireOp",EDGE,"E87"),sQuery(id+"F0.wireOp",EDGE,"E88"),sQuery(id+"F0.wireOp",EDGE,"E89"),sQuery(id+"F0.wireOp",EDGE,"E90"),sQuery(id+"F0.wireOp",EDGE,"E91"),sQuery(id+"F0.wireOp",EDGE,"E92"),sQuery(id+"F0.wireOp",EDGE,"E93"),sQuery(id+"F0.wireOp",EDGE,"E94"),sQuery(id+"F0.wireOp",EDGE,"E95"),sQuery(id+"F0.wireOp",EDGE,"E96"),sQuery(id+"F0.wireOp",EDGE,"E97"),sQuery(id+"F0.wireOp",EDGE,"E98"),sQuery(id+"F0.wireOp",EDGE,"E99"),sQuery(id+"F0.wireOp",EDGE,"E100"),sQuery(id+"F0.wireOp",EDGE,"E101"),sQuery(id+"F0.wireOp",EDGE,"E102"),sQuery(id+"F0.wireOp",EDGE,"E103"),sQuery(id+"F0.wireOp",EDGE,"E104"),sQuery(id+"F0.wireOp",EDGE,"E105"),sQuery(id+"F0.wireOp",EDGE,"E106"),sQuery(id+"F0.wireOp",EDGE,"E107"),sQuery(id+"F0.wireOp",EDGE,"E108"),sQuery(id+"F0.wireOp",EDGE,"E109"),sQuery(id+"F0.wireOp",EDGE,"E110"),sQuery(id+"F0.wireOp",EDGE,"E111"),sQuery(id+"F0.wireOp",EDGE,"E112"),sQuery(id+"F0.wireOp",EDGE,"E113"),sQuery(id+"F0.wireOp",EDGE,"E114"),sQuery(id+"F0.wireOp",EDGE,"E115"),sQuery(id+"F0.wireOp",EDGE,"E116"),sQuery(id+"F0.wireOp",EDGE,"E117"),sQuery(id+"F0.wireOp",EDGE,"E118"),sQuery(id+"F0.wireOp",EDGE,"E119"),sQuery(id+"F0.wireOp",EDGE,"E120"),sQuery(id+"F0.wireOp",EDGE,"E121"),sQuery(id+"F0.wireOp",EDGE,"E122"),sQuery(id+"F0.wireOp",EDGE,"E123"),sQuery(id+"F0.wireOp",EDGE,"E124.top"),sQuery(id+"F0.wireOp",EDGE,"E124.right"),sQuery(id+"F0.wireOp",EDGE,"E125.top"),sQuery(id+"F0.wireOp",EDGE,"E125.right"),sQuery(id+"F0.wireOp",EDGE,"E126"),sQuery(id+"F0.wireOp",EDGE,"E127"),sQuery(id+"F0.wireOp",EDGE,"E128"),sQuery(id+"F0.wireOp",EDGE,"E129")])]}),"instanceName":"1"});
            deleteBodies(context, id + "F16", {"entities" : qUnion([Q0])});
        }
        {
            var Q0;
            Q0=makeQuery(id+"F0.imprint","IMPRINT",FACE,{"disambiguationData":[TD([[makeQuery(id+"F0.imprint","IMPRINT",EDGE,{"derivedFrom":sQuery(id+"F0.wireOp",EDGE,"E0")}),-1.0]])]});
            extrude(context, id + "F17", {"entities" : qUnion([Q0]), "depth" : 100 * mm});
        }
        {
            var Q0;
            {var subQ0=sQuery(id+"F2.wireOp",EDGE,"E131.top");Q0=makeQuery(id+"F2.imprint","IMPRINT",FACE,{"disambiguationData":[TD([[makeQuery(id+"F2.imprint","IMPRINT",EDGE,{"derivedFrom":subQ0}),1.0]])]});}
            var Q1;
            Q1=makeQuery(id+"F2.imprint","IMPRINT",FACE,{"disambiguationData":[TD([[makeQuery(id+"F2.imprint","IMPRINT",EDGE,{"derivedFrom":sQuery(id+"F2.wireOp",EDGE,"E134.top")}),-1.0]])]});
            var Q2;
            Q2=makeQuery(id+"F2.imprint","IMPRINT",FACE,{"disambiguationData":[TD([[makeQuery(id+"F2.imprint","IMPRINT",EDGE,{"derivedFrom":sQuery(id+"F2.wireOp",EDGE,"E134.bottom")}),-1.0]])]});
            extrude(context, id + "F18", {"entities" : qUnion([Q0, Q1, Q2]), "depth" : 10 * mm});
        }
        {
            var Q0;
            {var subQ0=sQuery(id+"F2.wireOp",EDGE,"E133");Q0=makeQuery(id+"F2.imprint","IMPRINT",FACE,{"disambiguationData":[TD([[makeQuery(id+"F2.imprint","IMPRINT",EDGE,{"derivedFrom":subQ0}),1.0]])]});}
            extrude(context, id + "F19", {"entities" : qUnion([Q0]), "operationType" : NewBodyOperationType.ADD, "depth" : 14 * mm});
        }
        {
            var Q0;
            Q0=qCreatedBy(makeId("Front.planeOp"),FACE);
            var sketch = newSketch(context, id + "F20", { "sketchPlane" : qUnion([Q0])});
            skLineSegment(sketch, "E283.bottom", {"start": v(-61.01, 50.83) * mm, "end": v(-21.01, 50.83) * mm});
            skLineSegment(sketch, "E283.top", {"start": v(-61.01, 30.83) * mm, "end": v(-51.01, 30.83) * mm});
            skLineSegment(sketch, "E283.left", {"start": v(-61.01, 50.83) * mm, "end": v(-61.01, 30.83) * mm});
            skLineSegment(sketch, "E283.right", {"start": v(-21.01, 50.83) * mm, "end": v(-21.01, 30.83) * mm});
            skLineSegment(sketch, "E284", {"start": v(-41.01, 40.83) * mm, "end": v(-51.01, 30.83) * mm});
            skPoint(sketch, "E285.orphan", {"position": v(-41.01, 40.83) * mm});
            skLineSegment(sketch, "E286", {"start": v(-41.01, 52.38) * mm, "end": v(-41.01, 24.45) * mm, "construction": true});
            skPoint(sketch, "E286.startSnap0", {"position": v(-41.01, 50.83) * mm});
            skPoint(sketch, "E286.endSnap0", {"position": v(-41.01, 30.83) * mm});
            skLineSegment(sketch, "E287.MirrorCS", {"start": v(-41.01, 40.83) * mm, "end": v(-31.01, 30.83) * mm});
            skLineSegment(sketch, "E288.trimOffspring", {"start": v(-31.01, 30.83) * mm, "end": v(-21.01, 30.83) * mm});
            skPoint(sketch, "E289.left.end.orphan", {"position": v(-38.94, 42.9) * mm});
            skPoint(sketch, "E289.bottom.start.orphan", {"position": v(-38.94, 40.83) * mm});
            skPoint(sketch, "E290.orphan", {"position": v(-43.08, 42.9) * mm});
            skPoint(sketch, "E291.MirrorCS.start.orphan", {"position": v(-43.08, 40.83) * mm});
            skSolve(sketch);
        }
        {
            var Q0;
            Q0=makeQuery(id+"F20.imprint","IMPRINT",FACE,{"disambiguationData":[TD([[makeQuery(id+"F20.imprint","IMPRINT",EDGE,{"derivedFrom":sQuery(id+"F20.wireOp",EDGE,"E283.bottom")}),-1.0]])]});
            extrude(context, id + "F21", {"entities" : qUnion([Q0]), "depth" : 40 * mm});
        }
        {
            var Q0;
            Q0=makeQuery(id+"F21.opExtrude","SWEPT_FACE",FACE,{"disambiguationData":[OSD([sQuery(id+"F20.wireOp",EDGE,"E283.bottom")])]});
            var sketch = newSketch(context, id + "F22", { "sketchPlane" : qUnion([Q0])});
            skCircle(sketch, "E292", {"center": v(-56.01, -5) * mm, "radius": 4 * mm});
            skCircle(sketch, "E293.0.1.0", {"center": v(-56.01, -35) * mm, "radius": 4 * mm});
            skCircle(sketch, "E293.1.0.0", {"center": v(-26.01, -5) * mm, "radius": 4 * mm});
            skCircle(sketch, "E293.1.1.0", {"center": v(-26.01, -35) * mm, "radius": 4 * mm});
            skLineSegment(sketch, "E293.direction1", {"start": v(-56.01, -5) * mm, "end": v(-26.01, -5) * mm, "construction": true});
            skLineSegment(sketch, "E293.direction2", {"start": v(-56.01, -5) * mm, "end": v(-56.01, -35) * mm, "construction": true});
            skSolve(sketch);
        }
        {
            var Q0;
            Q0=makeQuery(id+"F22.imprint","IMPRINT",FACE,{"disambiguationData":[TD([[makeQuery(id+"F22.imprint","IMPRINT",EDGE,{"derivedFrom":sQuery(id+"F22.wireOp",EDGE,"E292")}),1.0]])]});
            var Q1;
            Q1=makeQuery(id+"F22.imprint","IMPRINT",FACE,{"disambiguationData":[TD([[makeQuery(id+"F22.imprint","IMPRINT",EDGE,{"derivedFrom":sQuery(id+"F22.wireOp",EDGE,"E293.1.0.0")}),1.0]])]});
            var Q2;
            Q2=makeQuery(id+"F22.imprint","IMPRINT",FACE,{"disambiguationData":[TD([[makeQuery(id+"F22.imprint","IMPRINT",EDGE,{"derivedFrom":sQuery(id+"F22.wireOp",EDGE,"E293.0.1.0")}),1.0]])]});
            var Q3;
            Q3=makeQuery(id+"F22.imprint","IMPRINT",FACE,{"disambiguationData":[TD([[makeQuery(id+"F22.imprint","IMPRINT",EDGE,{"derivedFrom":sQuery(id+"F22.wireOp",EDGE,"E293.1.1.0")}),1.0]])]});
            extrude(context, id + "F23", {"entities" : qUnion([Q0, Q1, Q2, Q3]), "operationType" : NewBodyOperationType.REMOVE, "endBound" : BoundingType.THROUGH_ALL, "oppositeDirection" : true, "depth" : 25 * mm});
        }
        {
            var Q0;
            Q0=makeQuery(id+"F21.opExtrude","SWEPT_FACE",FACE,{"disambiguationData":[OSD([sQuery(id+"F20.wireOp",EDGE,"E283.left")])]});
            var sketch = newSketch(context, id + "F24", { "sketchPlane" : qUnion([Q0])});
            skCircle(sketch, "E294", {"center": v(20, 40.83) * mm, "radius": 3.25 * mm});
            skLineSegment(sketch, "E295", {"start": v(0, 40.83) * mm, "end": v(40, 40.83) * mm, "construction": true});
            skLineSegment(sketch, "E296", {"start": v(20, 50.83) * mm, "end": v(20, 30.83) * mm});
            skSolve(sketch);
        }
        {
            var Q0;
            {var subQ0=sQuery(id+"F24.wireOp",EDGE,"E296");var subQ1=sQuery(id+"F24.wireOp",EDGE,"E294");var subQ2=makeQuery(id+"F24.imprint","INTERSECT",VERTEX,{"disambiguationData":[OD(0.0)],"derivedFrom":[subQ1,subQ0]});Q0=makeQuery(id+"F24.imprint","IMPRINT",FACE,{"disambiguationData":[TD([[makeQuery(id+"F24.imprint","IMPRINT",EDGE,{"disambiguationData":[TD([[subQ2,1.0]])],"derivedFrom":subQ1}),1.0]])]});}
            var Q1;
            {var subQ0=sQuery(id+"F24.wireOp",EDGE,"E296");var subQ1=sQuery(id+"F24.wireOp",EDGE,"E294");var subQ2=makeQuery(id+"F24.imprint","INTERSECT",VERTEX,{"disambiguationData":[OD(0.0)],"derivedFrom":[subQ1,subQ0]});Q1=makeQuery(id+"F24.imprint","IMPRINT",FACE,{"disambiguationData":[TD([[makeQuery(id+"F24.imprint","IMPRINT",EDGE,{"disambiguationData":[TD([[subQ2,-1.0]])],"derivedFrom":subQ1}),1.0]])]});}
            extrude(context, id + "F25", {"entities" : qUnion([Q0, Q1]), "operationType" : NewBodyOperationType.REMOVE, "oppositeDirection" : true, "depth" : 15 * mm});
        }
        {
            var Q0;
            Q0=qCreatedBy(makeId("Front.planeOp"),FACE);
            var sketch = newSketch(context, id + "F26", { "sketchPlane" : qUnion([Q0])});
            skCircle(sketch, "E297", {"center": v(0, 0) * mm, "radius": 12.5 * mm});
            skSolve(sketch);
        }
        {
            var Q0;
            Q0=qCreatedBy(makeId("Right.planeOp"),FACE);
            var sketch = newSketch(context, id + "F27", { "sketchPlane" : qUnion([Q0])});
            skLineSegment(sketch, "E298", {"start": v(-21.83, 14.06) * mm, "end": v(23.2, 14.06) * mm});
            skLineSegment(sketch, "E299", {"start": v(23.2, 14.06) * mm, "end": v(23.2, 5.19) * mm});
            skLineSegment(sketch, "E300", {"start": v(23.2, 5.19) * mm, "end": v(-21.83, 5.19) * mm});
            skLineSegment(sketch, "E301", {"start": v(-21.83, 5.19) * mm, "end": v(-21.83, 14.06) * mm});
            skLineSegment(sketch, "E302", {"start": v(-4.75, 5.19) * mm, "end": v(-4.75, 14.06) * mm});
            skLineSegment(sketch, "E303", {"start": v(5.25, 14.06) * mm, "end": v(5.25, 5.19) * mm});
            skLineSegment(sketch, "E304", {"start": v(0, 27.66) * mm, "end": v(0, -7.5) * mm, "construction": true});
            skSolve(sketch);
        }
        {
            var Q0;
            Q0=makeQuery(id+"F26.imprint","IMPRINT",FACE,{"disambiguationData":[TD([[makeQuery(id+"F26.imprint","IMPRINT",EDGE,{"derivedFrom":sQuery(id+"F26.wireOp",EDGE,"E297")}),1.0]])]});
            extrude(context, id + "F28", {"entities" : qUnion([Q0]), "endBound" : BoundingType.SYMMETRIC, "depth" : 160 * mm});
        }
        {
            var Q0;
            {var subQ0=sQuery(id+"F27.wireOp",EDGE,"E299");Q0=makeQuery(id+"F27.imprint","IMPRINT",FACE,{"disambiguationData":[TD([[makeQuery(id+"F27.imprint","IMPRINT",EDGE,{"derivedFrom":subQ0}),-1.0]])]});}
            var Q1;
            {var subQ0=sQuery(id+"F27.wireOp",EDGE,"E301");Q1=makeQuery(id+"F27.imprint","IMPRINT",FACE,{"disambiguationData":[TD([[makeQuery(id+"F27.imprint","IMPRINT",EDGE,{"derivedFrom":subQ0}),-1.0]])]});}
            extrude(context, id + "F29", {"entities" : qUnion([Q0, Q1]), "operationType" : NewBodyOperationType.REMOVE, "endBound" : BoundingType.THROUGH_ALL, "oppositeDirection" : true, "depth" : 25 * mm, "hasSecondDirection" : true, "secondDirectionBound" : SecondDirectionBoundingType.THROUGH_ALL, "secondDirectionOppositeDirection" : false, "secondDirectionDepth" : 25 * mm});
        }
        {
            var Q0;
            Q0=qCreatedBy(makeId("Top.planeOp"),FACE);
            var sketch = newSketch(context, id + "F30", { "sketchPlane" : qUnion([Q0])});
            skCircle(sketch, "E305", {"center": v(0, 0) * mm, "radius": 4 * mm});
            skSolve(sketch);
        }
        {
            var Q0;
            Q0=makeQuery(id+"F30.imprint","IMPRINT",FACE,{"disambiguationData":[TD([[makeQuery(id+"F30.imprint","IMPRINT",EDGE,{"derivedFrom":sQuery(id+"F30.wireOp",EDGE,"E305")}),1.0]])]});
            extrude(context, id + "F31", {"entities" : qUnion([Q0]), "operationType" : NewBodyOperationType.REMOVE, "endBound" : BoundingType.THROUGH_ALL, "oppositeDirection" : true, "depth" : 25 * mm, "hasSecondDirection" : true, "secondDirectionBound" : SecondDirectionBoundingType.THROUGH_ALL, "secondDirectionOppositeDirection" : false, "secondDirectionDepth" : 25 * mm});
        }
    });
